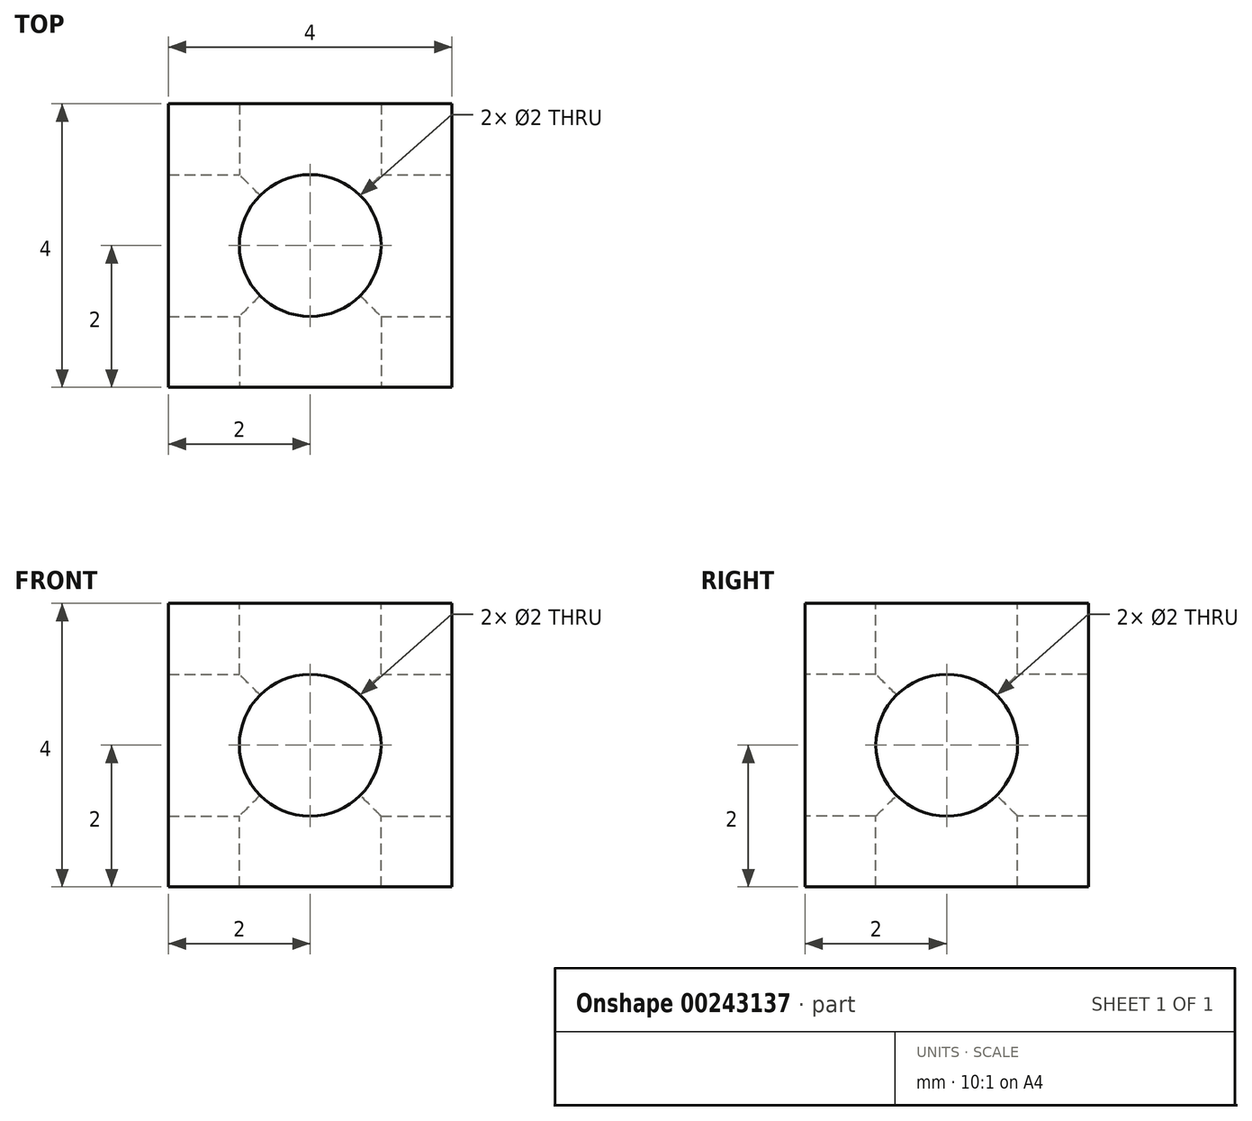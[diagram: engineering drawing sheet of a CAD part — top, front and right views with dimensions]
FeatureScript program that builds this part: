
annotation { "Feature Type Name" : "Feature", "Feature Type Description" : "" }
export const myFeature = defineFeature(function(context is Context, id is Id, definition is map)
    precondition{}
    {
        {
            var Q0;
            Q0=qCreatedBy(makeId("Front.planeOp"),FACE);
            var sketch = newSketch(context, id + "F0", { "sketchPlane" : qUnion([Q0])});
            skLineSegment(sketch, "E0.bottom", {"start": v(0, 0) * mm, "end": v(4, 0) * mm});
            skLineSegment(sketch, "E0.top", {"start": v(0, 4) * mm, "end": v(4, 4) * mm});
            skLineSegment(sketch, "E0.left", {"start": v(0, 0) * mm, "end": v(0, 4) * mm});
            skLineSegment(sketch, "E0.right", {"start": v(4, 0) * mm, "end": v(4, 4) * mm});
            skSolve(sketch);
        }
        {
            var Q0;
            Q0 = qSketchRegion(id + "F0", true);
            extrude(context, id + "F1", {"entities" : qUnion([Q0]), "depth" : 4 * mm});
        }
        {
            var Q0;
            Q0=makeQuery(id+"F1.opExtrude","CAP_FACE",FACE,{"disambiguationData":[OSD([sQuery(id+"F0.wireOp",EDGE,"E0.bottom"),sQuery(id+"F0.wireOp",EDGE,"E0.top"),sQuery(id+"F0.wireOp",EDGE,"E0.left"),sQuery(id+"F0.wireOp",EDGE,"E0.right")])],"isStart":false});
            var sketch = newSketch(context, id + "F2", { "sketchPlane" : qUnion([Q0])});
            skLineSegment(sketch, "E1", {"start": v(2, 4) * mm, "end": v(2, 0) * mm, "construction": true});
            skCircle(sketch, "E2", {"center": v(2, 2) * mm, "radius": 1 * mm});
            skSolve(sketch);
        }
        {
            var Q0;
            Q0 = qSketchRegion(id + "F2", true);
            extrude(context, id + "F3", {"entities" : qUnion([Q0]), "operationType" : NewBodyOperationType.REMOVE, "oppositeDirection" : true, "depth" : 4 * mm});
        }
        {
            var Q0;
            Q0=makeQuery(id+"F1.opExtrude","SWEPT_FACE",FACE,{"disambiguationData":[OSD([sQuery(id+"F0.wireOp",EDGE,"E0.right")])]});
            var sketch = newSketch(context, id + "F4", { "sketchPlane" : qUnion([Q0])});
            skLineSegment(sketch, "E3", {"start": v(-2, 4) * mm, "end": v(-2, 0) * mm, "construction": true});
            skCircle(sketch, "E4", {"center": v(-2, 2) * mm, "radius": 1 * mm});
            skSolve(sketch);
        }
        {
            var Q0;
            Q0 = qSketchRegion(id + "F4", true);
            extrude(context, id + "F5", {"entities" : qUnion([Q0]), "operationType" : NewBodyOperationType.REMOVE, "oppositeDirection" : true, "depth" : 4 * mm});
        }
        {
            var Q0;
            Q0=makeQuery(id+"F1.opExtrude","SWEPT_FACE",FACE,{"disambiguationData":[OSD([sQuery(id+"F0.wireOp",EDGE,"E0.top")])]});
            var sketch = newSketch(context, id + "F6", { "sketchPlane" : qUnion([Q0])});
            skLineSegment(sketch, "E5", {"start": v(0, -2) * mm, "end": v(4, -2) * mm, "construction": true});
            skCircle(sketch, "E6", {"center": v(2, -2) * mm, "radius": 1 * mm});
            skSolve(sketch);
        }
        {
            var Q0;
            Q0 = qSketchRegion(id + "F6", true);
            extrude(context, id + "F7", {"entities" : qUnion([Q0]), "operationType" : NewBodyOperationType.REMOVE, "oppositeDirection" : true, "depth" : 4 * mm});
        }
    });
